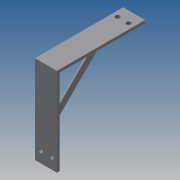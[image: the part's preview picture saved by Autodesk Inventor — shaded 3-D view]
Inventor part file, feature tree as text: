
AUTODESK INVENTOR PART (.ipt)
format: ipt  version: 2014 SP1 (Build 180222100, 222)  size: 106,496 bytes
history: native  units: in
note: dims shown in document units (in); Inventor stores cm internally (conversion verified against a paired STEP export)
features: sketch x4, extrude x2, hole x2, plane x1
ambient origin geometry x8: Origin, YZ Plane, XZ Plane, XY Plane, X Axis, Y Axis, Z Axis, Center Point
bodies: Solid1 (feature_tree)
feature tree (9):
  extrude  "Extrusion1"  Depth=4.0in
  plane  "Work Plane1"
  extrude  "Extrusion2"  Depth=1.0in TaperAngle=0.0deg
  hole  "Hole1"  [1 undecoded]
  hole  "Hole2"  [1 undecoded]
  sketch  "Sketch1"  dims[d0=4.0in d1=4.0in]
  sketch  "Sketch2"  dims[d2=0.125in d3=1.0in d4=0.0in]
  sketch  "Sketch4"  dims[d5=-0.5in d6=45.0deg]
  sketch  "Sketch5"  dims[d7=0.3123in d8=0.07in d9=0.0in d10=0.5in d11=0.25in d12=0.7874in d14=0.5in d15=0.3937in d17=1.0in d19=0.201in d20=0.75in d21=0.385in d22=0.25in d23=0.5635in d24=1.0in d25=0.8108in d26=0.5in d27=0.25in d28=0.7874in d30=0.5in d31=0.3937in d33=1.0in d35=0.201in d36=0.75in d37=0.385in d38=0.25in d39=0.5635in d40=1.0in d41=0.8108in]
note: 2 required parameter values undecoded (feature->parameter linkage not recoverable at this tier; creation-order binding heuristic only, values carry confidence <= 0.55)
